# Revit family: Wall-Panel_Operable-Partition_Moderco_Signature-Series
name_source: partatom
category: Curtain Panels
units: mm (PartAtom-declared; Revit-internal decimal feet)

## family parameters
Always vertical = Yes
Cut with Voids When Loaded = No
OmniClass Number = 23.25.40.17
OmniClass Title = Operable Partitions
Shared = No

## types (5) — shared parameters
Assembly Code = C1010300
Construction Details = http://www.arcat.com
Keynote = 10 22 26
Manufacturer = Moderco, Inc
Manufacturer Fax = 450-641-4965 or 800-231-4965
Manufacturer Website = http://moderco.com
Panel Thickness = 0' - 4"
Product Data = http://www.arcat.com
Revision = R1_2015-09
Sales Information = http://moderco.com
Specification = http://www.arcat.com
URL = http://moderco.com
zero-valued in all types: Expected Lifespan (Years), Maintenance Schedule (Months), Warranty Duration (Years)

## per-type parameters (varying)
| type | Description | Max Height | Model | Use |
| 8760 Electric Panel | Moderco Signature Series 8760 Single Wall Panel as Specified | 16' - 4" | 8760 | Electric |
| 8720 Electric Panel | Moderco Signature Series 8720 Single Wall Panel as Specified | 16' - 4" | 8720 | Electric |
| 8500 Paired Panel | Moderco Signature Series 8500 Paired Wall Panel as Specified | 22' - 4" | 8500 | Pair |
| 8800 Single Panel | Moderco Signature Series 8800 Single Wall Panel as Specified | 30' - 4" | 8800 | Single |
| 8600 Single Panel | Moderco Signature Series 8600 Single Wall Panel as Specified | 22' - 4" | 8600 | Single |

## geometry (parser evidence)
native form markers: Sweep x3
no freeform markers — native parametric forms only
